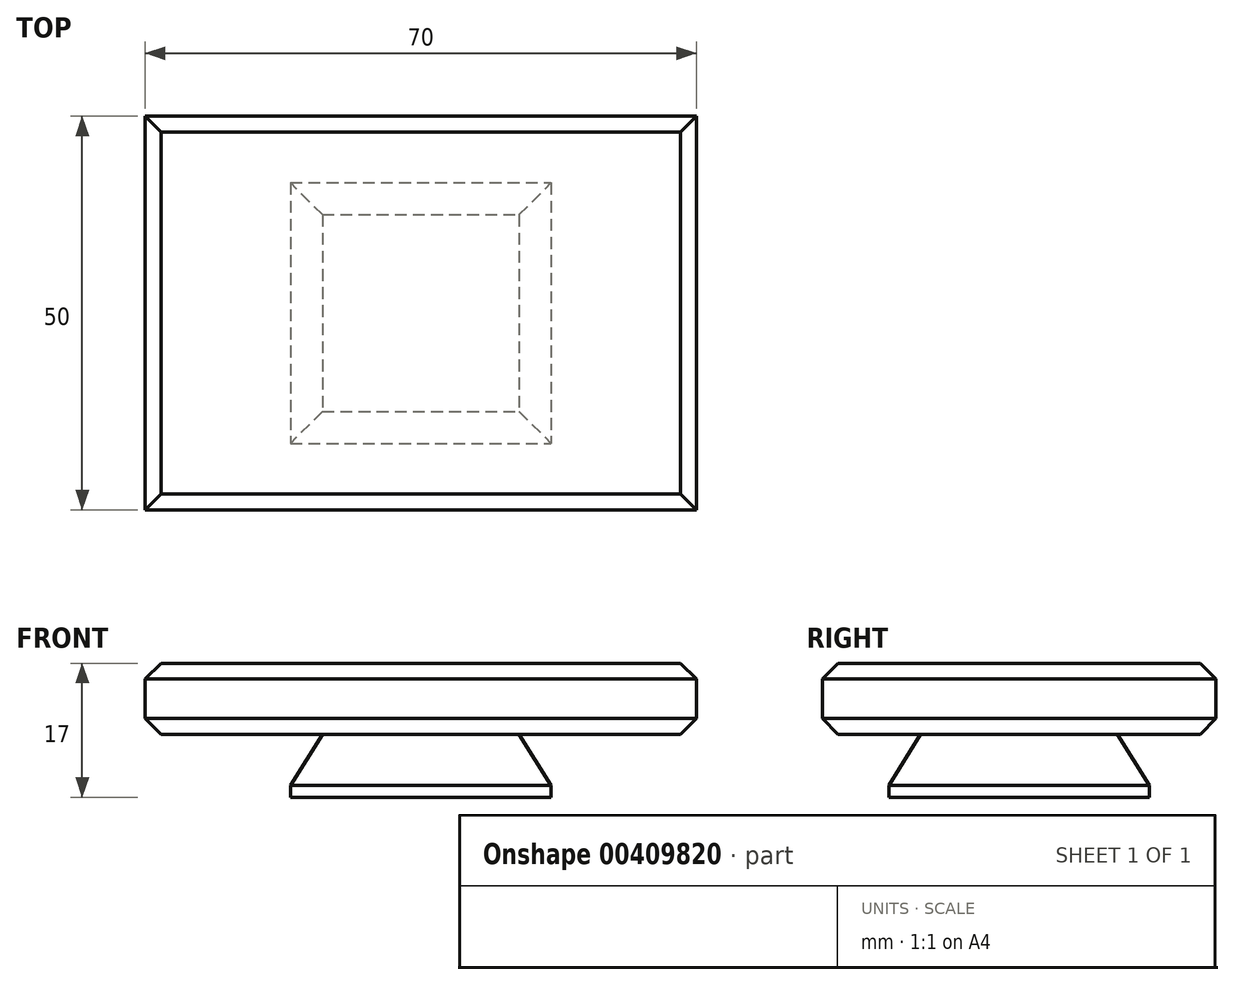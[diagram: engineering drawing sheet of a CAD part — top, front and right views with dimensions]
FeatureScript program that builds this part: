
annotation { "Feature Type Name" : "Feature", "Feature Type Description" : "" }
export const myFeature = defineFeature(function(context is Context, id is Id, definition is map)
    precondition{}
    {
        {
            var Q0;
            Q0=qCreatedBy(makeId("Top.planeOp"),FACE);
            var sketch = newSketch(context, id + "F0", { "sketchPlane" : qUnion([Q0])});
            skLineSegment(sketch, "E0.bottom", {"start": v(35, 25) * mm, "end": v(-35, 25) * mm});
            skLineSegment(sketch, "E0.top", {"start": v(35, -25) * mm, "end": v(-35, -25) * mm});
            skLineSegment(sketch, "E0.left", {"start": v(35, 25) * mm, "end": v(35, -25) * mm});
            skLineSegment(sketch, "E0.right", {"start": v(-35, 25) * mm, "end": v(-35, -25) * mm});
            skPoint(sketch, "E0.middle", {"position": v(0, 0) * mm});
            skSolve(sketch);
        }
        {
            var Q0;
            Q0 = qSketchRegion(id + "F0", true);
            extrude(context, id + "F1", {"entities" : qUnion([Q0]), "depth" : 9 * mm});
        }
        {
            var Q0;
            Q0=makeQuery(id+"F1.opExtrude","CAP_FACE",FACE,{"disambiguationData":[OSD([sQuery(id+"F0.wireOp",EDGE,"E0.bottom"),sQuery(id+"F0.wireOp",EDGE,"E0.top"),sQuery(id+"F0.wireOp",EDGE,"E0.left"),sQuery(id+"F0.wireOp",EDGE,"E0.right")])],"isStart":true});
            var sketch = newSketch(context, id + "F2", { "sketchPlane" : qUnion([Q0])});
            skLineSegment(sketch, "E1.bottom", {"start": v(17.5, 17.5) * mm, "end": v(-17.5, 17.5) * mm});
            skLineSegment(sketch, "E1.top", {"start": v(17.5, -17.5) * mm, "end": v(-17.5, -17.5) * mm});
            skLineSegment(sketch, "E1.left", {"start": v(17.5, 17.5) * mm, "end": v(17.5, -17.5) * mm});
            skLineSegment(sketch, "E1.right", {"start": v(-17.5, 17.5) * mm, "end": v(-17.5, -17.5) * mm});
            skPoint(sketch, "E1.middle", {"position": v(0, 0) * mm});
            skSolve(sketch);
        }
        {
            var Q0;
            Q0 = qSketchRegion(id + "F2", true);
            extrude(context, id + "F3", {"entities" : qUnion([Q0]), "operationType" : NewBodyOperationType.ADD, "depth" : 8 * mm});
        }
        {
            var Q0;
            Q0=qCreatedBy(makeId("Front.planeOp"),FACE);
            var sketch = newSketch(context, id + "F4", { "sketchPlane" : qUnion([Q0])});
            skLineSegment(sketch, "E2.0", {"start": v(17.5, -8) * mm, "end": v(-17.5, -8) * mm, "construction": true});
            skLineSegment(sketch, "E3", {"start": v(16.56, -6.5) * mm, "end": v(12.5, 0) * mm});
            skLineSegment(sketch, "E4", {"start": v(12.5, 0) * mm, "end": v(17.5, 0) * mm});
            skLineSegment(sketch, "E5", {"start": v(17.5, 0) * mm, "end": v(17.5, -8) * mm});
            skLineSegment(sketch, "E6", {"start": v(0, 0) * mm, "end": v(0, 16.99) * mm, "construction": true});
            skLineSegment(sketch, "E7.MirrorCS", {"start": v(-12.5, 0) * mm, "end": v(-17.5, 0) * mm});
            skLineSegment(sketch, "E8.MirrorCS", {"start": v(-16.56, -6.5) * mm, "end": v(-12.5, 0) * mm});
            skLineSegment(sketch, "E9.MirrorCS", {"start": v(-17.5, 0) * mm, "end": v(-17.5, -8) * mm});
            skLineSegment(sketch, "E10", {"start": v(16.56, -6.5) * mm, "end": v(16.56, -10.54) * mm});
            skLineSegment(sketch, "E11.MirrorCS", {"start": v(-16.56, -6.5) * mm, "end": v(-16.56, -10.54) * mm});
            skLineSegment(sketch, "E12", {"start": v(-17.5, -8) * mm, "end": v(-16.56, -8) * mm});
            skLineSegment(sketch, "E13", {"start": v(17.5, -8) * mm, "end": v(16.56, -8) * mm});
            skSolve(sketch);
        }
        {
            var Q0;
            Q0 = qSketchRegion(id + "F4", true);
            extrude(context, id + "F5", {"entities" : qUnion([Q0]), "operationType" : NewBodyOperationType.REMOVE, "oppositeDirection" : true, "depth" : 25 * mm, "hasSecondDirection" : true, "secondDirectionOppositeDirection" : false, "secondDirectionDepth" : 25 * mm});
        }
        {
            var Q0;
            Q0=qCreatedBy(makeId("Right.planeOp"),FACE);
            var sketch = newSketch(context, id + "F6", { "sketchPlane" : qUnion([Q0])});
            skLineSegment(sketch, "E14", {"start": v(12.5, 0) * mm, "end": v(16.56, -6.5) * mm});
            skLineSegment(sketch, "E15", {"start": v(17.5, -8) * mm, "end": v(17.5, 0) * mm});
            skLineSegment(sketch, "E16", {"start": v(17.5, 0) * mm, "end": v(12.5, 0) * mm});
            skLineSegment(sketch, "E17", {"start": v(0, 0) * mm, "end": v(0, 15.13) * mm, "construction": true});
            skLineSegment(sketch, "E18.MirrorCS", {"start": v(-17.5, -8) * mm, "end": v(-17.5, 0) * mm});
            skLineSegment(sketch, "E19.MirrorCS", {"start": v(-12.5, 0) * mm, "end": v(-16.56, -6.5) * mm});
            skLineSegment(sketch, "E20.MirrorCS", {"start": v(-17.5, 0) * mm, "end": v(-12.5, 0) * mm});
            skLineSegment(sketch, "E21", {"start": v(16.56, -6.5) * mm, "end": v(16.56, -9.87) * mm});
            skLineSegment(sketch, "E22", {"start": v(16.56, -6.5) * mm, "end": v(20.6, -6.5) * mm});
            skLineSegment(sketch, "E23.MirrorCS", {"start": v(-16.56, -6.5) * mm, "end": v(-16.56, -9.87) * mm});
            skLineSegment(sketch, "E24", {"start": v(-17.5, -8) * mm, "end": v(-16.56, -8) * mm});
            skLineSegment(sketch, "E25", {"start": v(17.5, -8) * mm, "end": v(16.56, -8) * mm});
            skSolve(sketch);
        }
        {
            var Q0;
            Q0 = qSketchRegion(id + "F6", true);
            extrude(context, id + "F7", {"entities" : qUnion([Q0]), "operationType" : NewBodyOperationType.REMOVE, "oppositeDirection" : true, "depth" : 25 * mm, "hasSecondDirection" : true, "secondDirectionOppositeDirection" : false, "secondDirectionDepth" : 25 * mm});
        }
        {
            var Q0;
            Q0=makeQuery(id+"F1.opExtrude","CAP_FACE",FACE,{"disambiguationData":[OSD([sQuery(id+"F0.wireOp",EDGE,"E0.bottom"),sQuery(id+"F0.wireOp",EDGE,"E0.top"),sQuery(id+"F0.wireOp",EDGE,"E0.left"),sQuery(id+"F0.wireOp",EDGE,"E0.right")])],"isStart":false});
            var Q1;
            Q1=makeQuery(id+"F1.opExtrude","CAP_EDGE",EDGE,{"disambiguationData":[OSD([sQuery(id+"F0.wireOp",EDGE,"E0.top")])],"isStart":true});
            var Q2;
            Q2=makeQuery(id+"F1.opExtrude","CAP_EDGE",EDGE,{"disambiguationData":[OSD([sQuery(id+"F0.wireOp",EDGE,"E0.left")])],"isStart":true});
            var Q3;
            Q3=makeQuery(id+"F1.opExtrude","CAP_EDGE",EDGE,{"disambiguationData":[OSD([sQuery(id+"F0.wireOp",EDGE,"E0.bottom")])],"isStart":true});
            var Q4;
            Q4=makeQuery(id+"F1.opExtrude","CAP_EDGE",EDGE,{"disambiguationData":[OSD([sQuery(id+"F0.wireOp",EDGE,"E0.right")])],"isStart":true});
            chamfer(context, id + "F8", {"entities" : qUnion([Q0, Q1, Q2, Q3, Q4]), "width" : 2 * mm, "tangentPropagation" : true});
        }
    });
